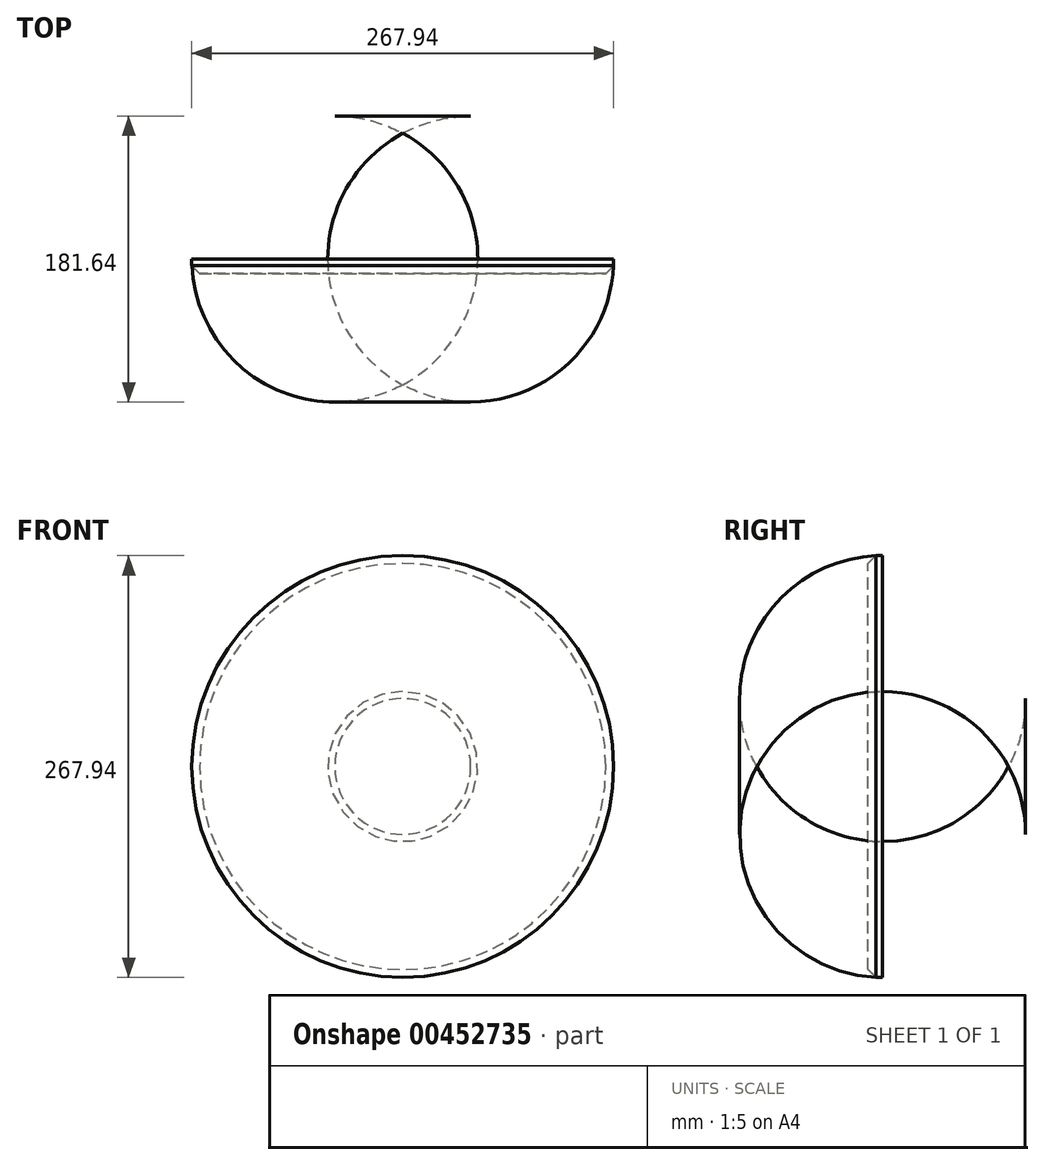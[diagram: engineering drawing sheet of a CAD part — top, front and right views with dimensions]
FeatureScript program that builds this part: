
annotation { "Feature Type Name" : "Feature", "Feature Type Description" : "" }
export const myFeature = defineFeature(function(context is Context, id is Id, definition is map)
    precondition{}
    {
        {
            var Q0;
            Q0=qCreatedBy(makeId("Front.planeOp"),FACE);
            var sketch = newSketch(context, id + "F0", { "sketchPlane" : qUnion([Q0])});
            skCircle(sketch, "E0", {"center": v(0, 0) * mm, "radius": 133.97 * mm});
            skSolve(sketch);
        }
        {
            var Q0;
            Q0 = qSketchRegion(id + "F0", true);
            extrude(context, id + "F1", {"entities" : qUnion([Q0]), "depth" : 100 * mm});
        }
        {
            var Q0;
            Q0=makeQuery(id+"F1.opExtrude","CAP_EDGE",EDGE,{"disambiguationData":[OSD([sQuery(id+"F0.wireOp",EDGE,"E0")])],"isStart":false});
            chamfer(context, id + "F2", {"entities" : qUnion([Q0]), "width" : 5 * mm, "tangentPropagation" : true});
        }
        {
            var Q0;
            Q0=makeQuery(id+"F1.opExtrude","CAP_EDGE",EDGE,{"disambiguationData":[OSD([sQuery(id+"F0.wireOp",EDGE,"E0")])],"isStart":true});
            var Q1;
            Q1=makeQuery(id+"F1.opExtrude","CAP_FACE",FACE,{"disambiguationData":[OSD([sQuery(id+"F0.wireOp",EDGE,"E0")])],"isStart":true});
            fillet(context, id + "F3", {"entities" : qUnion([Q0, Q1]), "radius" : 90.82 * mm, "tangentPropagation" : true, "allowEdgeOverflow" : false});
        }
    });
